# Revit family: Sanitary_Accessories_Sanindusa_New-WC-Care-70-Hand-Bar
name_source: partatom
category: Plumbing Fixtures
revit_build: Autodesk Revit 2018 (Build: 20170223_1515(x64)
units: mm (PartAtom-declared; Revit-internal decimal feet)

## family parameters
Always vertical = Yes
Cut with Voids When Loaded = No
OmniClass Number = 23.45.00.00
OmniClass Title = Sanitary, Laundry, and Cleaning Equipment
Part Type = Normal
Room Calculation Point = No
Round Connector Dimension = Use Diameter
Shared = No
Work Plane-Based = No

## types (1)
- Sanitary_Accessories_Sanindusa_New-WC-Care-70-Hand-Bar
    AssetType = Fixed
    BarCode = 5604815900354
    Color = Silver
    Constituents = Fixings not included
150 mm PVC flexible hose; ABS shower bracket, with adjustable height; Fixing Kit.
    Cost = 0 $
    Description = New Wccare hand bar
    Edition number = 1
    Element Type = GRAB BAR: Basic drop-down grab bar, for people with reduced mobility
    Features = Straight grab bar for people with reduced mobility. 
Tube Ø 35mm. For use as a handrail and grab bar for WCs, showers or baths. 
Stainless steel tube for easy maintenance and hygiene. 
40mm gap between the bar and the wall: minimal space prevents the forearm passing between the bar and the wall, reducing the risk of fracture in case of loss of balance.
    Finish = Brushed
    Installation Instructions = https://www.tec.sanindusa.pt
    InstallationDate = 1900-12-31T23:59:59
    Manufacturer = Sanindusa
    ManufacturerName = Sanindusa
    ManufacturerURL = www.tec.sanindusa.pt
    Material = Stainless steel
    ModelNumber = 4297013
    ModelReference = New Wccare
    Name = 70 hand bar new wccare
    NominalHeight = 0 mm  [stored 0 ft]
    NominalLength = 700 mm  [stored 2.29659 ft]
    NominalWidth = 116 mm  [stored 0.380577 ft]
    Pre-defined type (IFC) = FURNISHING ELEMENT
    Product Guid = 5102fc74-8fce-442f-ac20-0dbde9531ad8
    Product data url = https://bimobject.com
    ProductInformation = https://www.tec.sanindusa.pt
    ProductionYear = 2017
    Size = 70x12
    Type (IFC) = IfcFurnitureType
    URL = www.tec.sanindusa.pt
    Uniclass2015Version = Products v1.6
    Version = 2
    WarrantyDescription = https://www.tec.sanindusa.pt
The warranty will come into force from the moment the warranty detachable bulletin that accompanies the product is received at Sanindusa or from the moment the product is sold to the distributer
Only if the customer issues a writen and justified (Country laws, state laws, commercial strategy) request to Sanindusa, may the above mentioned warranties be the object of a possible change.
    WarrantyDurationParts = 5
    WarrantyDurationUnit = year
    WarrantyStartDate = 1900-12-31T23:59:59
1900-12-31T23:59:59
    Weight = 1.42 kg

note: [stored X ft] marks values corroborated as IEEE doubles in the binary element streams (Revit-internal decimal feet)

## geometry (parser evidence)
native form markers: Sweep x6
no freeform markers — native parametric forms only
